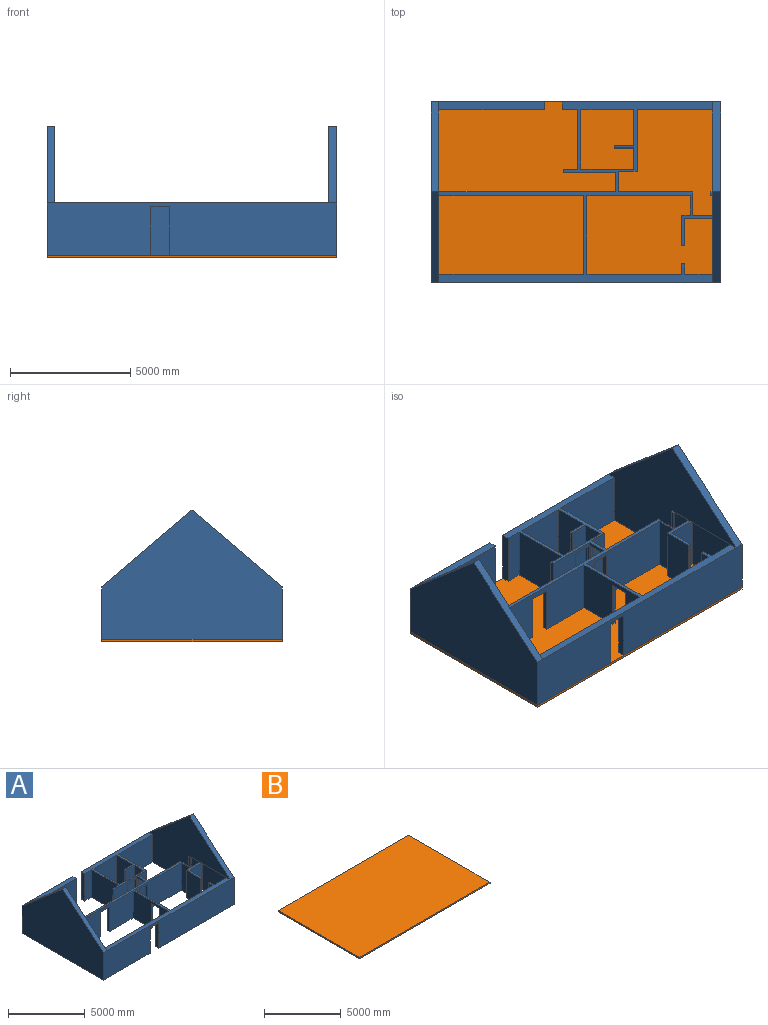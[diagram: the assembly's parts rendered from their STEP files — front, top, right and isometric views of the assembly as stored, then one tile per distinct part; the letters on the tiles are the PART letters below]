
ASSEMBLY  parts=2 mates=1
PART A: 84 faces, bbox 12039.6x7493x5384.8 mm
  f0: plane 11372.85x7493mm, normal (0,0,1), area 9327037.8mm2, adj f7,f9,f10,f11,f12,f13,f14,f15
  f1: plane 139.7x76.2mm, normal (0,0,1), area 10645.1mm2, adj f30,f31,f32,f33
  f2: plane 4375.15x317.5mm, normal (0,0,1), area 1389110.1mm2, adj f61,f65,f66,f67
  f3: plane 2006.6x127mm, normal (1,0,0), area 254838.2mm2, adj f15,f16,f58,f77
  f4: plane 2019.3x133.35mm, normal (0,-1,0), area 269273.7mm2, adj f25,f26,f58,f76
  f5: plane 2019.3x152.4mm, normal (1,0,0), area 307741.3mm2, adj f41,f64,f72,f75
  f6: plane 2032x317.5mm, normal (-1,0,0), area 645160mm2, adj f7,f57,f58,f69
  f7: plane 12039.6x2184.4mm, normal (0,-1,0), area 24699305.4mm2, adj f0,f6,f8,f58,f59,f60,f68,f69
  f8: plane 7493x5384.8mm, normal (1,0,0), area 28358007.8mm2, adj f7,f9,f58,f81,f82
  f9: plane 6584.95x2184.4mm, normal (0,1,0), area 14384164.8mm2, adj f0,f8,f10,f58,f81
  f10: plane 2184.4x317.5mm, normal (-1,0,0), area 693547mm2, adj f0,f9,f11,f58
  f11: plane 2184.4x641.35mm, normal (0,-1,0), area 1400964.9mm2, adj f0,f10,f12,f58
  f12: plane 2476.5x2184.4mm, normal (-1,0,0), area 5409666.6mm2, adj f0,f11,f13,f58
  f13: plane 2184.4x596.9mm, normal (0,1,0), area 1303868.4mm2, adj f0,f12,f14,f58
  f14: plane 2184.4x127mm, normal (-1,0,0), area 277418.8mm2, adj f0,f13,f15,f58
  f15: plane 2184.4x2159mm, normal (0,-1,0), area 3072413.2mm2, adj f0,f3,f14,f24,f25,f58,f77
  f16: plane 2190.75x2184.4mm, normal (0,1,0), area 3141767.9mm2, adj f0,f3,f17,f23,f24,f58,f77
  f17: plane 2476.5x2184.4mm, normal (1,0,0), area 5409666.6mm2, adj f0,f16,f18,f58
  f18: plane 2190.75x2184.4mm, normal (0,-1,0), area 4785474.3mm2, adj f0,f17,f19,f58
  f19: plane 2184.4x1485.9mm, normal (-1,0,0), area 3245800mm2, adj f0,f18,f20,f58
  f20: plane 2184.4x793.75mm, normal (0,1,0), area 1733867.5mm2, adj f0,f19,f21,f58
  f21: plane 2184.4x114.3mm, normal (-1,0,0), area 249676.9mm2, adj f0,f20,f22,f58
  f22: plane 2184.4x793.75mm, normal (0,-1,0), area 1733867.5mm2, adj f0,f21,f23,f58
  f23: plane 2184.4x876.3mm, normal (-1,0,0), area 1914189.7mm2, adj f0,f16,f22,f58
  f24: plane 2006.6x127mm, normal (-1,0,0), area 254838.2mm2, adj f15,f16,f58,f77
  f25: plane 2184.4x977.9mm, normal (-1,0,0), area 572256.9mm2, adj f0,f4,f15,f40,f41,f58,f64,f75
  f26: plane 2184.4x863.6mm, normal (1,0,0), area 347741.2mm2, adj f0,f4,f27,f39,f40,f58,f76
  f27: plane 2184.4x768.35mm, normal (0,-1,0), area 1678383.7mm2, adj f0,f26,f28,f58
  f28: plane 2565.4x2184.4mm, normal (1,0,0), area 5603859.8mm2, adj f0,f27,f29,f58
  f29: plane 3130.55x2184.4mm, normal (0,-1,0), area 6838373.4mm2, adj f0,f28,f30,f58
  f30: plane 7493x5384.8mm, normal (-1,0,0), area 19480606.2mm2, adj f0,f1,f29,f31,f58,f80,f81,f82
  f31: plane 2184.4x76.2mm, normal (0,1,0), area 166451.3mm2, adj f1,f30,f32,f58
  f32: plane 2184.4x139.7mm, normal (-1,0,0), area 305160.7mm2, adj f1,f31,f33,f58
  f33: plane 2184.4x88.9mm, normal (0,-1,0), area 194193.2mm2, adj f1,f32,f34,f58,f83
  f34: plane 2184.4x819.15mm, normal (-1,0,0), area 1789351.3mm2, adj f33,f35,f58,f83
  f35: plane 2184.4x850.9mm, normal (0,1,0), area 1858706mm2, adj f0,f34,f36,f58,f83
  f36: plane 2184.4x819.15mm, normal (1,0,0), area 1789351.3mm2, adj f0,f35,f37,f58
  f37: plane 2184.4x25.4mm, normal (0,-1,0), area 55483.8mm2, adj f0,f36,f38,f58
  f38: plane 2184.4x139.7mm, normal (1,0,0), area 305160.7mm2, adj f0,f37,f39,f58
  f39: plane 3086.1x2184.4mm, normal (0,1,0), area 6741276.8mm2, adj f0,f26,f38,f58
  f40: plane 2019.3x133.35mm, normal (0,1,0), area 269273.7mm2, adj f25,f26,f58,f76
  f41: plane 4305.3x2184.4mm, normal (0,-1,0), area 7955548.6mm2, adj f0,f5,f25,f42,f54,f58,f72,f75
  f42: plane 2184.4x812.8mm, normal (-1,0,0), area 1775480.3mm2, adj f0,f41,f43,f58
  f43: plane 2184.4x368.3mm, normal (0,1,0), area 804514.5mm2, adj f0,f42,f44,f58
  f44: plane 2184.4x1276.35mm, normal (-1,0,0), area 2788058.9mm2, adj f0,f43,f45,f58
  f45: plane 2184.4x127mm, normal (0,-1,0), area 277418.8mm2, adj f0,f44,f46,f58
  f46: plane 2184.4x1143mm, normal (1,0,0), area 2496769.2mm2, adj f0,f45,f47,f58
  f47: plane 2184.4x1244.6mm, normal (0,-1,0), area 2718704.2mm2, adj f0,f46,f48,f58,f80
  f48: plane 2330.45x2184.4mm, normal (-1,0,0), area 5090635mm2, adj f47,f49,f58,f80
  f49: plane 2184.4x1244.6mm, normal (0,1,0), area 2718704.2mm2, adj f0,f48,f50,f58,f80
  f50: plane 2184.4x438.15mm, normal (1,0,0), area 957094.9mm2, adj f0,f49,f51,f58
  f51: plane 2184.4x127mm, normal (0,1,0), area 277418.8mm2, adj f0,f50,f52,f58
  f52: plane 2184.4x438.15mm, normal (-1,0,0), area 957094.9mm2, adj f0,f51,f53,f58
  f53: plane 3937x2184.4mm, normal (0,1,0), area 8599982.8mm2, adj f0,f52,f54,f58
  f54: plane 3276.6x2184.4mm, normal (1,0,0), area 5612730.7mm2, adj f0,f41,f53,f55,f58,f70,f72,f73
  f55: plane 1993.9x139.7mm, normal (0,1,0), area 278547.8mm2, adj f54,f56,f58,f73
  f56: plane 3276.6x2184.4mm, normal (-1,0,0), area 5612730.7mm2, adj f0,f55,f57,f58,f62,f70,f72,f73
  f57: plane 6019.8x2184.4mm, normal (0,1,0), area 11549654.3mm2, adj f0,f6,f56,f58,f59,f61,f68,f69
  f58: plane 7493x6946.9mm, normal (0,0,-1), area 8537563.6mm2, adj f3,f4,f6,f7,f8,f9,f10,f11
  f59: plane 2032x317.5mm, normal (1,0,0), area 645160mm2, adj f7,f57,f68,f69
  f60: plane 7493x5384.8mm, normal (-1,0,0), area 28358007.8mm2, adj f7,f67,f68,f78,f79
  f61: plane 7493x5384.8mm, normal (1,0,0), area 26638011.2mm2, adj f0,f2,f57,f62,f64,f65,f68,f78
  f62: plane 6019.8x2184.4mm, normal (0,-1,0), area 11572396.2mm2, adj f0,f56,f61,f63,f68,f71,f72,f74
  f63: plane 1955.8x152.4mm, normal (1,0,0), area 298063.9mm2, adj f62,f64,f68,f74
  f64: plane 7340.6x2184.4mm, normal (0,1,0), area 13008603mm2, adj f0,f5,f25,f61,f63,f68,f71,f72
  f65: plane 4375.15x2184.4mm, normal (0,-1,0), area 9557077.7mm2, adj f2,f61,f66,f68
  f66: plane 2184.4x317.5mm, normal (1,0,0), area 693547mm2, adj f2,f65,f67,f68
  f67: plane 4692.65x2184.4mm, normal (0,1,0), area 10250624.7mm2, adj f2,f60,f66,f68,f78
  f68: plane 7493x4692.65mm, normal (0,0,-1), area 5492972.9mm2, adj f7,f57,f59,f60,f61,f62,f63,f64
  f69: plane 787.4x317.5mm, normal (0,0,-1), area 249999.5mm2, adj f6,f7,f57,f59
  f70: plane 1993.9x139.7mm, normal (0,-1,0), area 278547.8mm2, adj f54,f56,f72,f73
  f71: plane 1955.8x152.4mm, normal (-1,0,0), area 298063.9mm2, adj f62,f64,f72,f74
  f72: plane 2806.7x1841.5mm, normal (0,0,-1), area 663708.3mm2, adj f5,f41,f54,f56,f62,f64,f70,f71
  f73: plane 774.7x139.7mm, normal (0,0,-1), area 108225.6mm2, adj f54,f55,f56,f70
  f74: plane 806.45x152.4mm, normal (0,0,-1), area 122903mm2, adj f62,f63,f64,f71
  f75: plane 717.55x152.4mm, normal (0,0,-1), area 109354.6mm2, adj f5,f25,f41,f64
  f76: plane 762x133.35mm, normal (0,0,-1), area 101612.7mm2, adj f4,f25,f26,f40
  f77: plane 819.15x127mm, normal (0,0,-1), area 104032mm2, adj f3,f15,f16,f24
  f78: plane 3746.5x3200.4mm, normal (0,0.65,0.76), area 1564435.1mm2, adj f60,f61,f67,f79
  f79: plane 3746.5x3200.4mm, normal (0,-0.65,0.76), area 1564435.1mm2, adj f7,f60,f61,f78
  f80: plane 2330.45x95.25mm, normal (0,0,-1), area 221975.4mm2, adj f30,f47,f48,f49
  f81: plane 3746.5x3200.4mm, normal (0,0.65,0.76), area 1720878.6mm2, adj f8,f9,f30,f82
  f82: plane 3746.5x3200.4mm, normal (0,-0.65,0.76), area 1720878.6mm2, adj f7,f8,f30,f81
  f83: plane 819.15x12.7mm, normal (0,0,-1), area 10403.2mm2, adj f30,f33,f34,f35
PART B: 6 faces, bbox 12039.6x7493x101.6 mm
  f0: plane 12039.6x101.6mm, normal (0,1,0), area 1223223.4mm2, adj f1,f3,f4,f5
  f1: plane 7493x101.6mm, normal (1,0,0), area 761288.8mm2, adj f0,f2,f4,f5
  f2: plane 12039.6x101.6mm, normal (0,-1,0), area 1223223.4mm2, adj f1,f3,f4,f5
  f3: plane 7493x101.6mm, normal (-1,0,0), area 761288.8mm2, adj f0,f2,f4,f5
  f4: plane 12039.6x7493mm, normal (0,0,-1), area 90212722.8mm2, adj f0,f1,f2,f3
  f5: plane 12039.6x7493mm, normal (0,0,1), area 90212722.8mm2, adj f0,f1,f2,f3
PLACE A t=(0,0,101.6)mm
PLACE B t=(0,0,101.6)mm
MATE fastened A.f68 <-> B.f5  axis (0,0,1) through (0,0,101.6)mm
